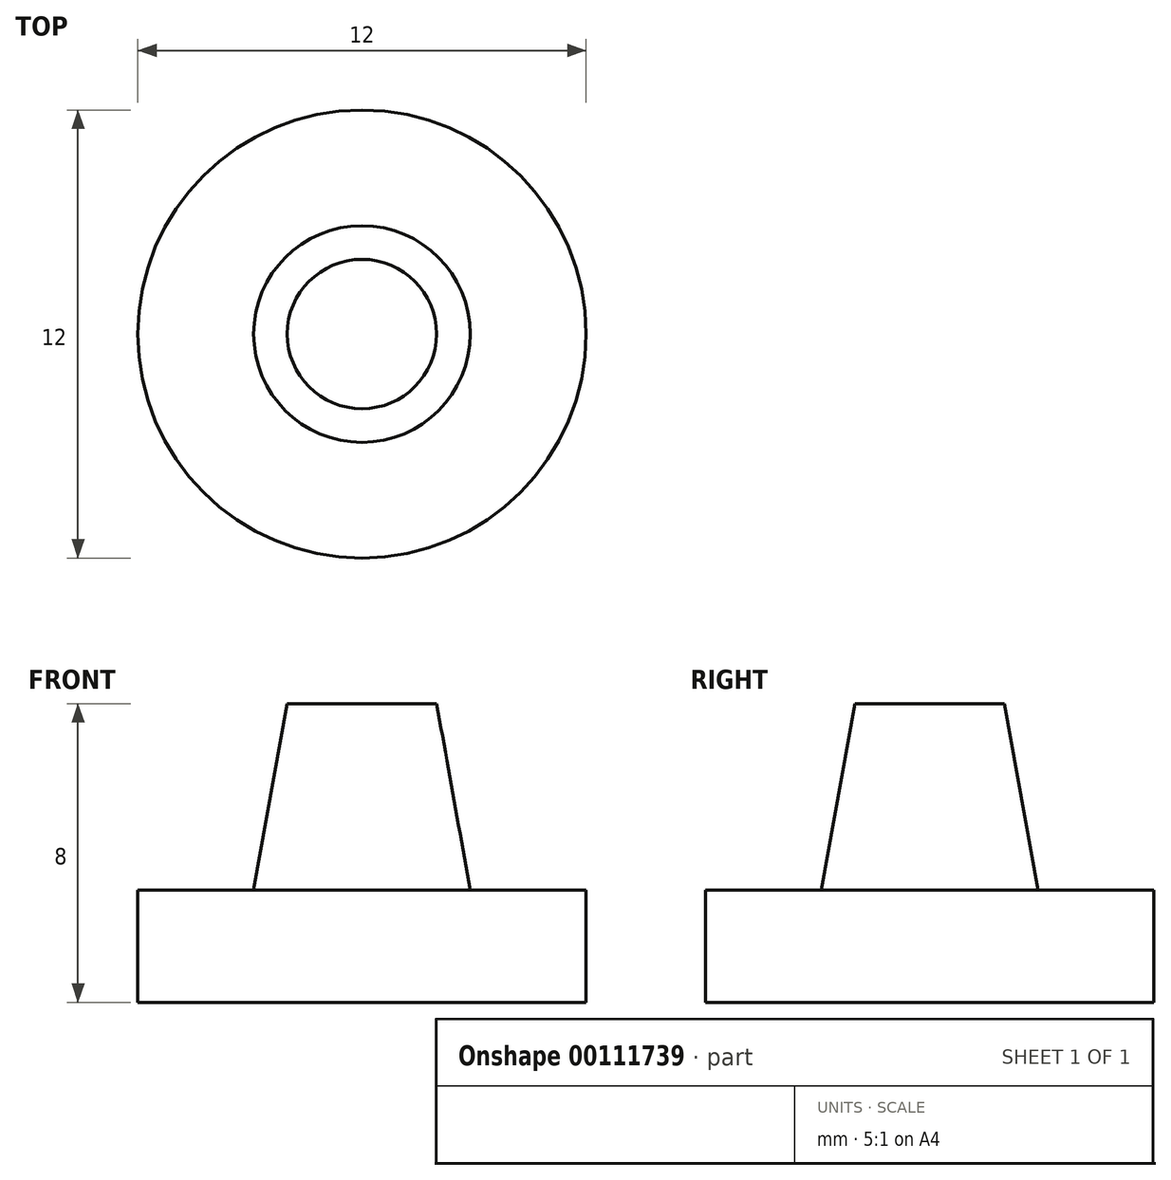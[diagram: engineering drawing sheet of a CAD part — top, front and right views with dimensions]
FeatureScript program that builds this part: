
annotation { "Feature Type Name" : "Feature", "Feature Type Description" : "" }
export const myFeature = defineFeature(function(context is Context, id is Id, definition is map)
    precondition{}
    {
        {
            var Q0;
            Q0=qCreatedBy(makeId("Front.planeOp"),FACE);
            var sketch = newSketch(context, id + "F0", { "sketchPlane" : qUnion([Q0])});
            skLineSegment(sketch, "E0", {"start": v(0, 0) * mm, "end": v(6, 0) * mm});
            skLineSegment(sketch, "E1", {"start": v(6, 0) * mm, "end": v(6, 3) * mm});
            skLineSegment(sketch, "E2", {"start": v(6, 3) * mm, "end": v(2.9, 3) * mm});
            skLineSegment(sketch, "E3", {"start": v(2, 8) * mm, "end": v(0, 8) * mm});
            skLineSegment(sketch, "E4", {"start": v(0, 8) * mm, "end": v(0, 0) * mm});
            skLineSegment(sketch, "E5", {"start": v(0, 21.2) * mm, "end": v(0, -4.86) * mm, "construction": true});
            skLineSegment(sketch, "E6", {"start": v(2.9, 3) * mm, "end": v(2, 8) * mm});
            skSolve(sketch);
        }
        {
            var Q0;
            Q0 = qSketchRegion(id + "F0", true);
            var Q1;
            Q1=sQuery(id+"F0.wireOp",EDGE,"E5");
            revolve(context, id + "F1", {"entities" : qUnion([Q0]), "axis" : qUnion([Q1]), "revolveType" : RevolveType.FULL});
        }
    });
